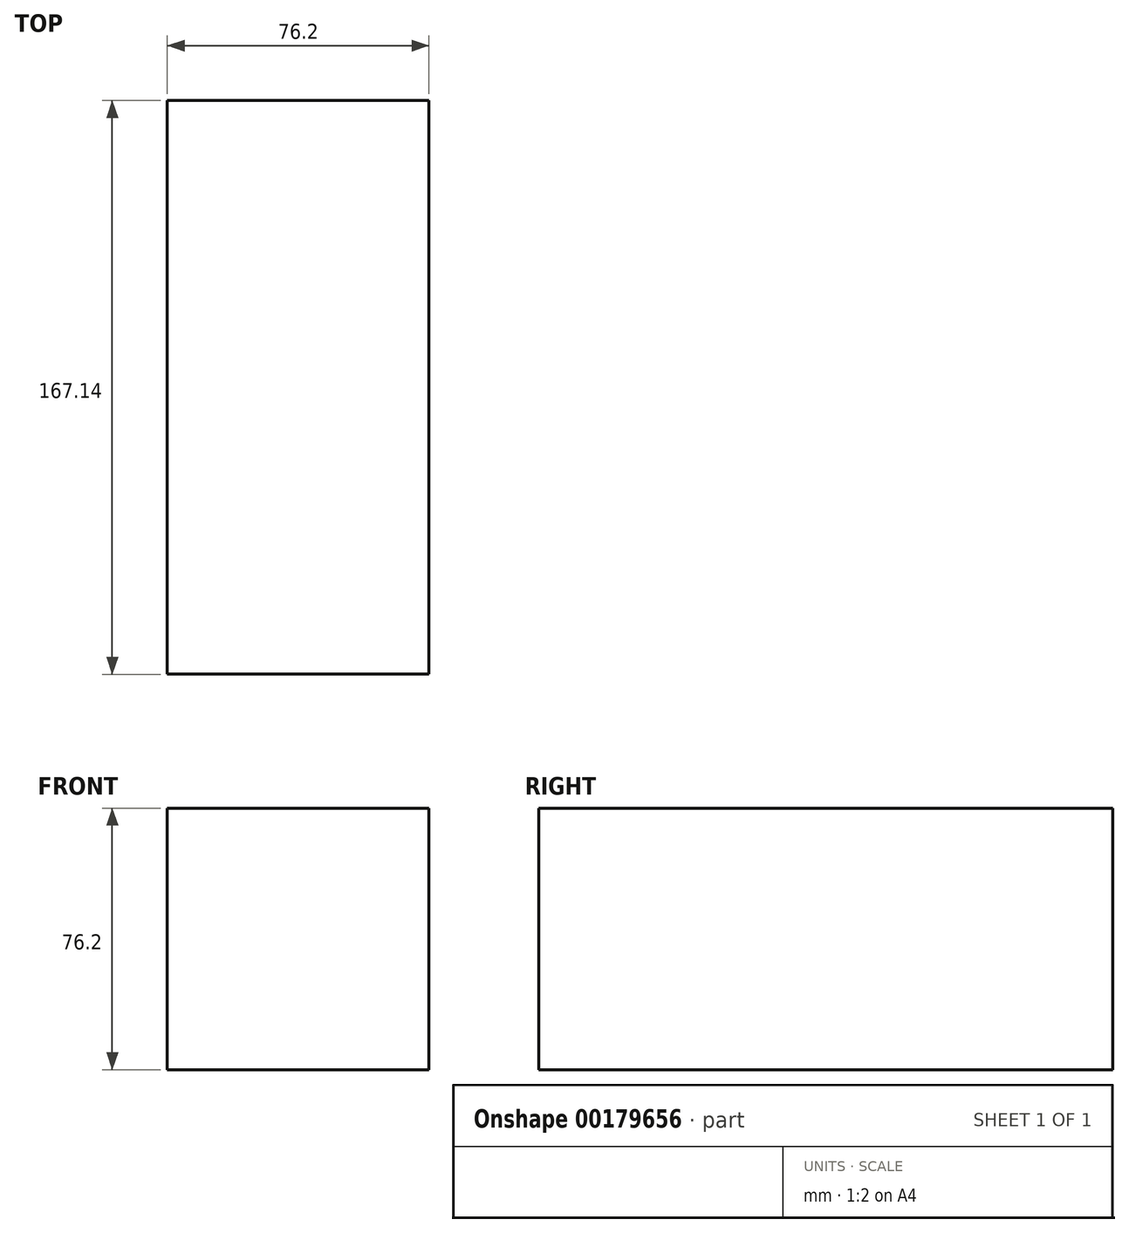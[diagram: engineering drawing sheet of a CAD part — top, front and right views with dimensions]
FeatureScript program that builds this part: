
annotation { "Feature Type Name" : "Feature", "Feature Type Description" : "" }
export const myFeature = defineFeature(function(context is Context, id is Id, definition is map)
    precondition{}
    {
        {
            var Q0;
            Q0=qCreatedBy(makeId("Front.planeOp"),FACE);
            var sketch = newSketch(context, id + "F0", { "sketchPlane" : qUnion([Q0])});
            skLineSegment(sketch, "E0.bottom", {"start": v(0, 0) * mm, "end": v(76.2, 0) * mm});
            skLineSegment(sketch, "E0.top", {"start": v(0, 76.2) * mm, "end": v(76.2, 76.2) * mm});
            skLineSegment(sketch, "E0.left", {"start": v(0, 0) * mm, "end": v(0, 76.2) * mm});
            skLineSegment(sketch, "E0.right", {"start": v(76.2, 0) * mm, "end": v(76.2, 76.2) * mm});
            skSolve(sketch);
        }
        {
            var Q0;
            Q0 = qSketchRegion(id + "F0", true);
            extrude(context, id + "F1", {"entities" : qUnion([Q0]), "flatOperationType" : FlatOperationType.REMOVE, "offsetDistance" : 25.4 * mm, "depth" : 167.13 * mm, "domain" : OperationDomain.MODEL, "symmetric" : true});
        }
    });
